# Revit family: 210_77f911a0648642ac96cdef31b31e94
name_source: partatom
category: Mechanical Equipment
revit_build: Autodesk Revit MEP 2015 (Build: 20160512_1515(x64)
units: mm (PartAtom-declared; Revit-internal decimal feet)

## types (2) — shared parameters
A = 169 mm  [stored 0.554462 ft]
D = 100 mm
Description = Centrifugal Jet fans
H = 150 mm  [stored 0.492126 ft]
L = 700 mm  [stored 2.29659 ft]
L2 = 350 mm  [stored 1.14829 ft]
Manufacturer = Systemair
N = 67 mm  [stored 0.219816 ft]
QmdConnectorList = 201;D
W = 500 mm
W2 = 251 mm  [stored 0.823491 ft]
magiPartTypeId = 210
magiProductFamilyId = 77f911a0648642ac96cdef31b31e94
zero-valued in all types: MC_Default_elevation

## per-type parameters (varying)
| type | magiProductId |
| IV Smart AC | 329cb2a1b5924f048e777494655bb3 |
| IV Smart EC | 797f7bd22a834d268ae501a220bda0 |

note: column(s) folded — value = type name in every type: magiProductCode

note: [stored X ft] marks values corroborated as IEEE doubles in the binary element streams (Revit-internal decimal feet)

## geometry (parser evidence)
native form markers: Sweep x2
no freeform markers — native parametric forms only
